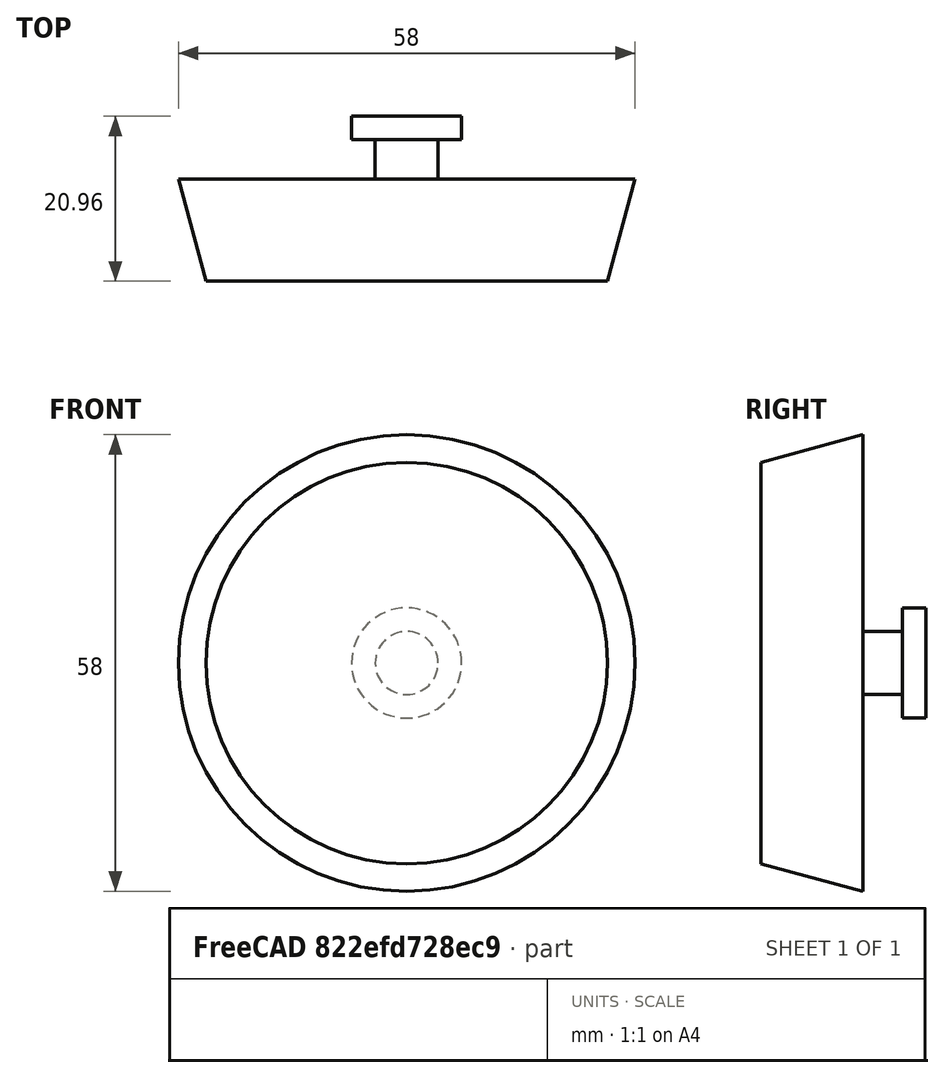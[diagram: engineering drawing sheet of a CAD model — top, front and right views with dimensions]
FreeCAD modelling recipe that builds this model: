
FCSTD DOCUMENT  (FreeCAD 0.19R24276 (Git))
Label: Tipa
License: All rights reserved
LicenseURL: http://en.wikipedia.org/wiki/All_rights_reserved
objects: Sketcher::SketchObject×1, PartDesign::Revolution×1, PartDesign::Body×1
note: 4 computed .brp shape members not serialized (recipe doc carries the construction recipe); baked Part::Feature solids carry a one-line shape summary decoded from their .brp

FEATURE [Sketcher::SketchObject] Sketch
  FullyConstrained = false
  MapMode = 5
  Support = -> [XY_Plane]
  sketch-geometry (9):
    g0: LineSegment StartX=0 StartY=0 StartZ=0 EndX=25.5 EndY=0 EndZ=0
    g1: LineSegment StartX=25.5 StartY=0 StartZ=0 EndX=29 EndY=12.961 EndZ=0
    g2: LineSegment StartX=29 StartY=12.961 StartZ=0 EndX=4 EndY=12.961 EndZ=0
    g3: LineSegment StartX=4 StartY=12.961 StartZ=0 EndX=4 EndY=17.961 EndZ=0
    g4: LineSegment StartX=4 StartY=17.961 StartZ=0 EndX=7 EndY=17.961 EndZ=0
    g5: LineSegment StartX=7 StartY=17.961 StartZ=0 EndX=7 EndY=20.961 EndZ=0
    g6: LineSegment StartX=7 StartY=20.961 StartZ=0 EndX=0 EndY=20.961 EndZ=0
    g7: LineSegment StartX=0 StartY=0 StartZ=0 EndX=0 EndY=20.961 EndZ=0
    g8: GeomPoint X=0 Y=0 Z=0
  constraints (23):
    c: Horizontal(g0)
    c: Coincident(g1,g0)
    c: Coincident(g2,g1)
    c: Horizontal(g2)
    c: DistanceX(g0,g1) = 29
    c: DistanceX(g0,g1) = 3.5
    c: DistanceX(g0,g2) = 4
    c: Coincident(g3,g2)
    c: Vertical(g3)
    c: Coincident(g4,g3)
    c: Horizontal(g4)
    c: Coincident(g5,g4)
    c: Vertical(g5)
    c: DistanceY(g2,g3) = 5
    c: DistanceX(g3,g4) = 3
    c: Coincident(g6,g5)
    c: Horizontal(g6)
    c: DistanceY(g4,g5) = 3
    c: Coincident(g7,g0)
    c: Coincident(g7,g6)
    c: Vertical(g7)
    c: Coincident(g0,g-1)
    c: Coincident(g8,g0)
FEATURE [PartDesign::Revolution] Revolution
  Angle = 360
  Axis = (0,1,0)
  Base = (0,0,0)
  Profile = -> Sketch
  ReferenceAxis = -> Sketch [V_Axis]
  Reversed = true
FEATURE [PartDesign::Body] Body
  Group = -> [Sketch,Revolution]
  Origin = -> Origin
  Tip = -> Revolution
